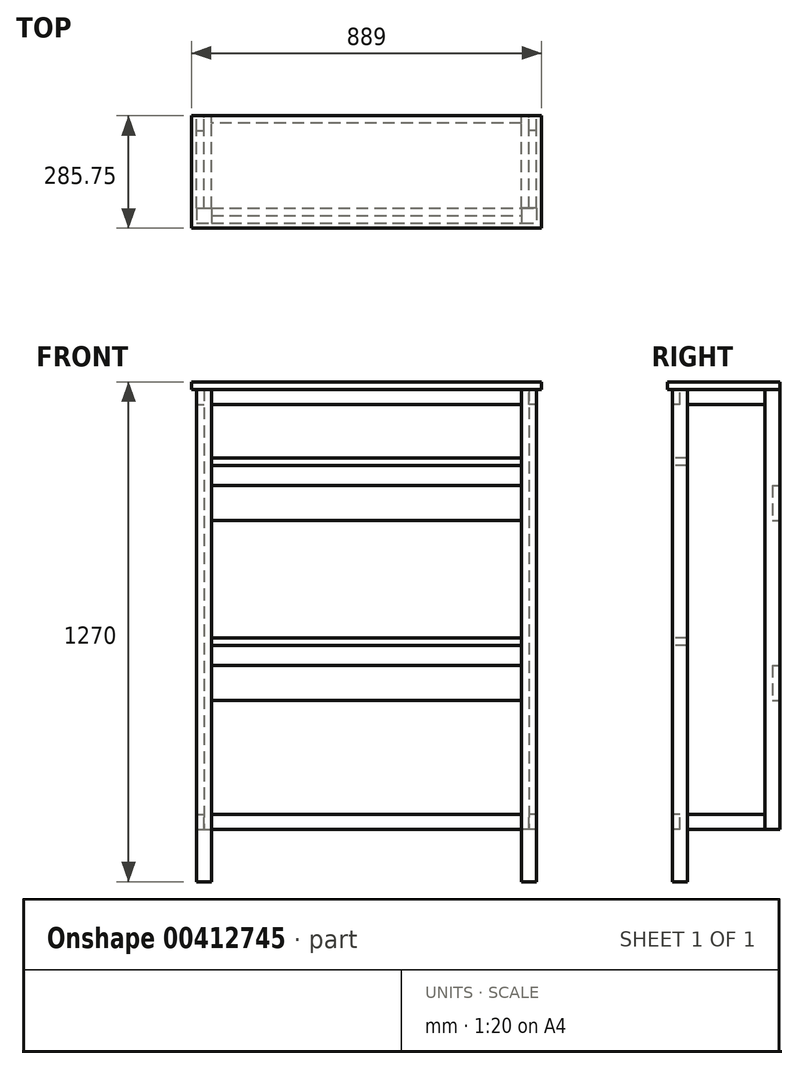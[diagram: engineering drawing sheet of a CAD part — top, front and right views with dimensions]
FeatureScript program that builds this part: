
annotation { "Feature Type Name" : "Feature", "Feature Type Description" : "" }
export const myFeature = defineFeature(function(context is Context, id is Id, definition is map)
    precondition{}
    {
        {
            var Q0;
            Q0=qCreatedBy(makeId("Front.planeOp"),FACE);
            var sketch = newSketch(context, id + "F0", { "sketchPlane" : qUnion([Q0])});
            skLineSegment(sketch, "E0.bottom", {"start": v(0, 0) * mm, "end": v(38.1, 0) * mm});
            skLineSegment(sketch, "E0.top", {"start": v(0, 1250.95) * mm, "end": v(38.1, 1250.95) * mm});
            skLineSegment(sketch, "E0.left", {"start": v(0, 0) * mm, "end": v(0, 1250.95) * mm});
            skLineSegment(sketch, "E0.right", {"start": v(38.1, 0) * mm, "end": v(38.1, 1250.95) * mm});
            skSolve(sketch);
        }
        {
            var Q0;
            Q0=makeQuery(id+"F0.imprint","IMPRINT",FACE,{"disambiguationData":[TD([[makeQuery(id+"F0.imprint","IMPRINT",EDGE,{"derivedFrom":sQuery(id+"F0.wireOp",EDGE,"E0.bottom")}),1.0]])]});
            extrude(context, id + "F1", {"entities" : qUnion([Q0]), "oppositeDirection" : true, "depth" : 38.1 * mm});
        }
        {
            var Q0;
            Q0=makeQuery(id+"F1.opExtrude","SWEPT_FACE",FACE,{"disambiguationData":[OSD([sQuery(id+"F0.wireOp",EDGE,"E0.right")])]});
            var sketch = newSketch(context, id + "F2", { "sketchPlane" : qUnion([Q0])});
            skLineSegment(sketch, "E1.bottom", {"start": v(38.1, 1250.95) * mm, "end": v(273.05, 1250.95) * mm});
            skLineSegment(sketch, "E1.top", {"start": v(38.1, 133.35) * mm, "end": v(273.05, 133.35) * mm});
            skLineSegment(sketch, "E1.left", {"start": v(38.1, 1250.95) * mm, "end": v(38.1, 133.35) * mm});
            skLineSegment(sketch, "E1.right", {"start": v(273.05, 1250.95) * mm, "end": v(273.05, 133.35) * mm});
            skSolve(sketch);
        }
        {
            var Q0;
            Q0=makeQuery(id+"F2.imprint","IMPRINT",FACE,{"disambiguationData":[TD([[makeQuery(id+"F2.imprint","IMPRINT",EDGE,{"derivedFrom":sQuery(id+"F2.wireOp",EDGE,"E1.bottom")}),-1.0]])]});
            extrude(context, id + "F3", {"entities" : qUnion([Q0]), "oppositeDirection" : true, "depth" : 19.05 * mm});
        }
        {
            var Q0;
            Q0=makeQuery(id+"F3.opExtrude","CAP_FACE",FACE,{"disambiguationData":[OSD([sQuery(id+"F2.wireOp",EDGE,"E1.bottom"),sQuery(id+"F2.wireOp",EDGE,"E1.top"),sQuery(id+"F2.wireOp",EDGE,"E1.left"),sQuery(id+"F2.wireOp",EDGE,"E1.right")])],"isStart":false});
            var sketch = newSketch(context, id + "F4", { "sketchPlane" : qUnion([Q0])});
            skLineSegment(sketch, "E2.bottom", {"start": v(-273.05, 1250.95) * mm, "end": v(-234.95, 1250.95) * mm});
            skLineSegment(sketch, "E2.top", {"start": v(-273.05, 133.35) * mm, "end": v(-234.95, 133.35) * mm});
            skLineSegment(sketch, "E2.left", {"start": v(-273.05, 1250.95) * mm, "end": v(-273.05, 133.35) * mm});
            skLineSegment(sketch, "E2.right", {"start": v(-234.95, 1250.95) * mm, "end": v(-234.95, 133.35) * mm});
            skSolve(sketch);
        }
        {
            var Q0;
            Q0=makeQuery(id+"F4.imprint","IMPRINT",FACE,{"disambiguationData":[TD([[makeQuery(id+"F4.imprint","IMPRINT",EDGE,{"derivedFrom":sQuery(id+"F4.wireOp",EDGE,"E2.bottom")}),1.0]])]});
            extrude(context, id + "F5", {"entities" : qUnion([Q0]), "depth" : 19.05 * mm});
        }
        {
            var Q0;
            Q0=makeQuery(id+"F3.opExtrude","CAP_FACE",FACE,{"disambiguationData":[OSD([sQuery(id+"F2.wireOp",EDGE,"E1.bottom"),sQuery(id+"F2.wireOp",EDGE,"E1.top"),sQuery(id+"F2.wireOp",EDGE,"E1.left"),sQuery(id+"F2.wireOp",EDGE,"E1.right")])],"isStart":false});
            var sketch = newSketch(context, id + "F6", { "sketchPlane" : qUnion([Q0])});
            skLineSegment(sketch, "E3.bottom", {"start": v(-234.95, 1250.95) * mm, "end": v(-38.1, 1250.95) * mm});
            skLineSegment(sketch, "E3.top", {"start": v(-234.95, 1212.85) * mm, "end": v(-38.1, 1212.85) * mm});
            skLineSegment(sketch, "E3.left", {"start": v(-234.95, 1250.95) * mm, "end": v(-234.95, 1212.85) * mm});
            skLineSegment(sketch, "E3.right", {"start": v(-38.1, 1250.95) * mm, "end": v(-38.1, 1212.85) * mm});
            skSolve(sketch);
        }
        {
            var Q0;
            Q0=makeQuery(id+"F6.imprint","IMPRINT",FACE,{"disambiguationData":[TD([[makeQuery(id+"F6.imprint","IMPRINT",EDGE,{"derivedFrom":sQuery(id+"F6.wireOp",EDGE,"E3.bottom")}),1.0]])]});
            extrude(context, id + "F7", {"entities" : qUnion([Q0]), "depth" : 19.05 * mm});
        }
        {
            var Q0;
            Q0=makeQuery(id+"F3.opExtrude","CAP_FACE",FACE,{"disambiguationData":[OSD([sQuery(id+"F2.wireOp",EDGE,"E1.bottom"),sQuery(id+"F2.wireOp",EDGE,"E1.top"),sQuery(id+"F2.wireOp",EDGE,"E1.left"),sQuery(id+"F2.wireOp",EDGE,"E1.right")])],"isStart":false});
            var sketch = newSketch(context, id + "F8", { "sketchPlane" : qUnion([Q0])});
            skLineSegment(sketch, "E4.bottom", {"start": v(-38.1, 133.35) * mm, "end": v(-234.95, 133.35) * mm});
            skLineSegment(sketch, "E4.top", {"start": v(-38.1, 171.45) * mm, "end": v(-234.95, 171.45) * mm});
            skLineSegment(sketch, "E4.left", {"start": v(-38.1, 133.35) * mm, "end": v(-38.1, 171.45) * mm});
            skLineSegment(sketch, "E4.right", {"start": v(-234.95, 133.35) * mm, "end": v(-234.95, 171.45) * mm});
            skSolve(sketch);
        }
        {
            var Q0;
            Q0=makeQuery(id+"F8.imprint","IMPRINT",FACE,{"disambiguationData":[TD([[makeQuery(id+"F8.imprint","IMPRINT",EDGE,{"derivedFrom":sQuery(id+"F8.wireOp",EDGE,"E4.bottom")}),-1.0]])]});
            extrude(context, id + "F9", {"entities" : qUnion([Q0]), "depth" : 19.05 * mm});
        }
        {
            var Q0;
            Q0=qCreatedBy(makeId("Front.planeOp"),FACE);
            var sketch = newSketch(context, id + "F10", { "sketchPlane" : qUnion([Q0])});
            skLineSegment(sketch, "E5.bottom", {"start": v(825.5, 0) * mm, "end": v(863.6, 0) * mm});
            skLineSegment(sketch, "E5.top", {"start": v(825.5, 1250.95) * mm, "end": v(863.6, 1250.95) * mm});
            skLineSegment(sketch, "E5.left", {"start": v(825.5, 0) * mm, "end": v(825.5, 1250.95) * mm});
            skLineSegment(sketch, "E5.right", {"start": v(863.6, 0) * mm, "end": v(863.6, 1250.95) * mm});
            skSolve(sketch);
        }
        {
            var Q0;
            Q0=makeQuery(id+"F10.imprint","IMPRINT",FACE,{"disambiguationData":[TD([[makeQuery(id+"F10.imprint","IMPRINT",EDGE,{"derivedFrom":sQuery(id+"F10.wireOp",EDGE,"E5.bottom")}),1.0]])]});
            extrude(context, id + "F11", {"entities" : qUnion([Q0]), "oppositeDirection" : true, "depth" : 38.1 * mm});
        }
        {
            var Q0;
            Q0=makeQuery(id+"F11.opExtrude","SWEPT_FACE",FACE,{"disambiguationData":[OSD([sQuery(id+"F10.wireOp",EDGE,"E5.left")])]});
            var sketch = newSketch(context, id + "F12", { "sketchPlane" : qUnion([Q0])});
            skLineSegment(sketch, "E6.bottom", {"start": v(-38.1, 1250.95) * mm, "end": v(-273.05, 1250.95) * mm});
            skLineSegment(sketch, "E6.top", {"start": v(-38.1, 133.35) * mm, "end": v(-273.05, 133.35) * mm});
            skLineSegment(sketch, "E6.left", {"start": v(-38.1, 1250.95) * mm, "end": v(-38.1, 133.35) * mm});
            skLineSegment(sketch, "E6.right", {"start": v(-273.05, 1250.95) * mm, "end": v(-273.05, 133.35) * mm});
            skSolve(sketch);
        }
        {
            var Q0;
            Q0=makeQuery(id+"F12.imprint","IMPRINT",FACE,{"disambiguationData":[TD([[makeQuery(id+"F12.imprint","IMPRINT",EDGE,{"derivedFrom":sQuery(id+"F12.wireOp",EDGE,"E6.bottom")}),1.0]])]});
            extrude(context, id + "F13", {"entities" : qUnion([Q0]), "oppositeDirection" : true, "depth" : 19.05 * mm});
        }
        {
            var Q0;
            Q0=makeQuery(id+"F13.opExtrude","CAP_FACE",FACE,{"disambiguationData":[OSD([sQuery(id+"F12.wireOp",EDGE,"E6.bottom"),sQuery(id+"F12.wireOp",EDGE,"E6.top"),sQuery(id+"F12.wireOp",EDGE,"E6.left"),sQuery(id+"F12.wireOp",EDGE,"E6.right")])],"isStart":false});
            var sketch = newSketch(context, id + "F14", { "sketchPlane" : qUnion([Q0])});
            skLineSegment(sketch, "E7.bottom", {"start": v(273.05, 1250.95) * mm, "end": v(234.95, 1250.95) * mm});
            skLineSegment(sketch, "E7.top", {"start": v(273.05, 133.35) * mm, "end": v(234.95, 133.35) * mm});
            skLineSegment(sketch, "E7.left", {"start": v(273.05, 1250.95) * mm, "end": v(273.05, 133.35) * mm});
            skLineSegment(sketch, "E7.right", {"start": v(234.95, 1250.95) * mm, "end": v(234.95, 133.35) * mm});
            skSolve(sketch);
        }
        {
            var Q0;
            Q0=makeQuery(id+"F14.imprint","IMPRINT",FACE,{"disambiguationData":[TD([[makeQuery(id+"F14.imprint","IMPRINT",EDGE,{"derivedFrom":sQuery(id+"F14.wireOp",EDGE,"E7.bottom")}),-1.0]])]});
            extrude(context, id + "F15", {"entities" : qUnion([Q0]), "depth" : 19.05 * mm});
        }
        {
            var Q0;
            Q0=makeQuery(id+"F13.opExtrude","CAP_FACE",FACE,{"disambiguationData":[OSD([sQuery(id+"F12.wireOp",EDGE,"E6.bottom"),sQuery(id+"F12.wireOp",EDGE,"E6.top"),sQuery(id+"F12.wireOp",EDGE,"E6.left"),sQuery(id+"F12.wireOp",EDGE,"E6.right")])],"isStart":false});
            var sketch = newSketch(context, id + "F16", { "sketchPlane" : qUnion([Q0])});
            skLineSegment(sketch, "E8.bottom", {"start": v(38.1, 1250.95) * mm, "end": v(234.95, 1250.95) * mm});
            skLineSegment(sketch, "E8.top", {"start": v(38.1, 1212.85) * mm, "end": v(234.95, 1212.85) * mm});
            skLineSegment(sketch, "E8.left", {"start": v(38.1, 1250.95) * mm, "end": v(38.1, 1212.85) * mm});
            skLineSegment(sketch, "E8.right", {"start": v(234.95, 1250.95) * mm, "end": v(234.95, 1212.85) * mm});
            skSolve(sketch);
        }
        {
            var Q0;
            Q0=makeQuery(id+"F16.imprint","IMPRINT",FACE,{"disambiguationData":[TD([[makeQuery(id+"F16.imprint","IMPRINT",EDGE,{"derivedFrom":sQuery(id+"F16.wireOp",EDGE,"E8.bottom")}),-1.0]])]});
            extrude(context, id + "F17", {"entities" : qUnion([Q0]), "depth" : 19.05 * mm});
        }
        {
            var Q0;
            Q0=makeQuery(id+"F13.opExtrude","CAP_FACE",FACE,{"disambiguationData":[OSD([sQuery(id+"F12.wireOp",EDGE,"E6.bottom"),sQuery(id+"F12.wireOp",EDGE,"E6.top"),sQuery(id+"F12.wireOp",EDGE,"E6.left"),sQuery(id+"F12.wireOp",EDGE,"E6.right")])],"isStart":false});
            var sketch = newSketch(context, id + "F18", { "sketchPlane" : qUnion([Q0])});
            skLineSegment(sketch, "E9.bottom", {"start": v(38.1, 171.45) * mm, "end": v(234.95, 171.45) * mm});
            skLineSegment(sketch, "E9.top", {"start": v(38.1, 133.35) * mm, "end": v(234.95, 133.35) * mm});
            skLineSegment(sketch, "E9.left", {"start": v(38.1, 171.45) * mm, "end": v(38.1, 133.35) * mm});
            skLineSegment(sketch, "E9.right", {"start": v(234.95, 171.45) * mm, "end": v(234.95, 133.35) * mm});
            skSolve(sketch);
        }
        {
            var Q0;
            Q0=makeQuery(id+"F18.imprint","IMPRINT",FACE,{"disambiguationData":[TD([[makeQuery(id+"F18.imprint","IMPRINT",EDGE,{"derivedFrom":sQuery(id+"F18.wireOp",EDGE,"E9.bottom")}),-1.0]])]});
            extrude(context, id + "F19", {"entities" : qUnion([Q0]), "depth" : 19.05 * mm});
        }
        {
            var Q0;
            Q0=makeQuery(id+"F1.opExtrude","CAP_FACE",FACE,{"disambiguationData":[OSD([sQuery(id+"F0.wireOp",EDGE,"E0.bottom"),sQuery(id+"F0.wireOp",EDGE,"E0.top"),sQuery(id+"F0.wireOp",EDGE,"E0.left"),sQuery(id+"F0.wireOp",EDGE,"E0.right")])],"isStart":true});
            var sketch = newSketch(context, id + "F20", { "sketchPlane" : qUnion([Q0])});
            skLineSegment(sketch, "E10.bottom", {"start": v(38.1, 1250.95) * mm, "end": v(825.5, 1250.95) * mm});
            skLineSegment(sketch, "E10.top", {"start": v(38.1, 1212.85) * mm, "end": v(825.5, 1212.85) * mm});
            skLineSegment(sketch, "E10.left", {"start": v(38.1, 1250.95) * mm, "end": v(38.1, 1212.85) * mm});
            skLineSegment(sketch, "E10.right", {"start": v(825.5, 1250.95) * mm, "end": v(825.5, 1212.85) * mm});
            skSolve(sketch);
        }
        {
            var Q0;
            Q0=makeQuery(id+"F20.imprint","IMPRINT",FACE,{"disambiguationData":[TD([[makeQuery(id+"F20.imprint","IMPRINT",EDGE,{"derivedFrom":sQuery(id+"F20.wireOp",EDGE,"E10.bottom")}),-1.0]])]});
            extrude(context, id + "F21", {"entities" : qUnion([Q0]), "oppositeDirection" : true, "depth" : 19.05 * mm});
        }
        {
            var Q0;
            Q0=makeQuery(id+"F1.opExtrude","CAP_FACE",FACE,{"disambiguationData":[OSD([sQuery(id+"F0.wireOp",EDGE,"E0.bottom"),sQuery(id+"F0.wireOp",EDGE,"E0.top"),sQuery(id+"F0.wireOp",EDGE,"E0.left"),sQuery(id+"F0.wireOp",EDGE,"E0.right")])],"isStart":true});
            var sketch = newSketch(context, id + "F22", { "sketchPlane" : qUnion([Q0])});
            skLineSegment(sketch, "E11.bottom", {"start": v(38.1, 133.35) * mm, "end": v(825.5, 133.35) * mm});
            skLineSegment(sketch, "E11.top", {"start": v(38.1, 171.45) * mm, "end": v(825.5, 171.45) * mm});
            skLineSegment(sketch, "E11.left", {"start": v(38.1, 133.35) * mm, "end": v(38.1, 171.45) * mm});
            skLineSegment(sketch, "E11.right", {"start": v(825.5, 133.35) * mm, "end": v(825.5, 171.45) * mm});
            skSolve(sketch);
        }
        {
            var Q0;
            Q0=makeQuery(id+"F22.imprint","IMPRINT",FACE,{"disambiguationData":[TD([[makeQuery(id+"F22.imprint","IMPRINT",EDGE,{"derivedFrom":sQuery(id+"F22.wireOp",EDGE,"E11.bottom")}),1.0]])]});
            extrude(context, id + "F23", {"entities" : qUnion([Q0]), "oppositeDirection" : true, "depth" : 19.05 * mm});
        }
        {
            var Q0;
            Q0=makeQuery(id+"F1.opExtrude","CAP_FACE",FACE,{"disambiguationData":[OSD([sQuery(id+"F0.wireOp",EDGE,"E0.bottom"),sQuery(id+"F0.wireOp",EDGE,"E0.top"),sQuery(id+"F0.wireOp",EDGE,"E0.left"),sQuery(id+"F0.wireOp",EDGE,"E0.right")])],"isStart":true});
            var sketch = newSketch(context, id + "F24", { "sketchPlane" : qUnion([Q0])});
            skLineSegment(sketch, "E12.bottom", {"start": v(38.1, 600.08) * mm, "end": v(825.5, 600.08) * mm});
            skLineSegment(sketch, "E12.top", {"start": v(38.1, 619.13) * mm, "end": v(825.5, 619.13) * mm});
            skLineSegment(sketch, "E12.left", {"start": v(38.1, 600.08) * mm, "end": v(38.1, 619.13) * mm});
            skLineSegment(sketch, "E12.right", {"start": v(825.5, 600.08) * mm, "end": v(825.5, 619.13) * mm});
            skPoint(sketch, "E13", {"position": v(38.1, 609.6) * mm});
            skSolve(sketch);
        }
        {
            var Q0;
            Q0=makeQuery(id+"F24.imprint","IMPRINT",FACE,{"disambiguationData":[TD([[makeQuery(id+"F24.imprint","IMPRINT",EDGE,{"derivedFrom":sQuery(id+"F24.wireOp",EDGE,"E12.bottom")}),1.0]])]});
            extrude(context, id + "F25", {"entities" : qUnion([Q0]), "oppositeDirection" : true, "depth" : 38.1 * mm});
        }
        {
            var Q0;
            Q0=makeQuery(id+"F1.opExtrude","CAP_FACE",FACE,{"disambiguationData":[OSD([sQuery(id+"F0.wireOp",EDGE,"E0.bottom"),sQuery(id+"F0.wireOp",EDGE,"E0.top"),sQuery(id+"F0.wireOp",EDGE,"E0.left"),sQuery(id+"F0.wireOp",EDGE,"E0.right")])],"isStart":true});
            var sketch = newSketch(context, id + "F26", { "sketchPlane" : qUnion([Q0])});
            skLineSegment(sketch, "E14.bottom", {"start": v(38.1, 1076.33) * mm, "end": v(825.5, 1076.33) * mm});
            skLineSegment(sketch, "E14.top", {"start": v(38.1, 1057.28) * mm, "end": v(825.5, 1057.28) * mm});
            skLineSegment(sketch, "E14.left", {"start": v(38.1, 1076.33) * mm, "end": v(38.1, 1057.28) * mm});
            skLineSegment(sketch, "E14.right", {"start": v(825.5, 1076.33) * mm, "end": v(825.5, 1057.28) * mm});
            skPoint(sketch, "E15", {"position": v(38.1, 1066.8) * mm});
            skSolve(sketch);
        }
        {
            var Q0;
            Q0=makeQuery(id+"F26.imprint","IMPRINT",FACE,{"disambiguationData":[TD([[makeQuery(id+"F26.imprint","IMPRINT",EDGE,{"derivedFrom":sQuery(id+"F26.wireOp",EDGE,"E14.bottom")}),-1.0]])]});
            extrude(context, id + "F27", {"entities" : qUnion([Q0]), "oppositeDirection" : true, "depth" : 38.1 * mm});
        }
        {
            var Q0;
            Q0=makeQuery(id+"F3.opExtrude","SWEPT_FACE",FACE,{"disambiguationData":[OSD([sQuery(id+"F2.wireOp",EDGE,"E1.right")])]});
            var sketch = newSketch(context, id + "F28", { "sketchPlane" : qUnion([Q0])});
            skLineSegment(sketch, "E16.bottom", {"start": v(-825.5, 1006.48) * mm, "end": v(-38.1, 1006.48) * mm});
            skLineSegment(sketch, "E16.top", {"start": v(-825.5, 917.58) * mm, "end": v(-38.1, 917.58) * mm});
            skLineSegment(sketch, "E16.left", {"start": v(-825.5, 1006.48) * mm, "end": v(-825.5, 917.58) * mm});
            skLineSegment(sketch, "E16.right", {"start": v(-38.1, 1006.48) * mm, "end": v(-38.1, 917.58) * mm});
            skSolve(sketch);
        }
        {
            var Q0;
            Q0=makeQuery(id+"F28.imprint","IMPRINT",FACE,{"disambiguationData":[TD([[makeQuery(id+"F28.imprint","IMPRINT",EDGE,{"derivedFrom":sQuery(id+"F28.wireOp",EDGE,"E16.bottom")}),-1.0]])]});
            extrude(context, id + "F29", {"entities" : qUnion([Q0]), "oppositeDirection" : true, "depth" : 19.05 * mm});
        }
        {
            var Q0;
            Q0=makeQuery(id+"F13.opExtrude","SWEPT_FACE",FACE,{"disambiguationData":[OSD([sQuery(id+"F12.wireOp",EDGE,"E6.right")])]});
            var sketch = newSketch(context, id + "F30", { "sketchPlane" : qUnion([Q0])});
            skLineSegment(sketch, "E17.bottom", {"start": v(-825.5, 549.28) * mm, "end": v(-38.1, 549.28) * mm});
            skLineSegment(sketch, "E17.top", {"start": v(-825.5, 460.38) * mm, "end": v(-38.1, 460.38) * mm});
            skLineSegment(sketch, "E17.left", {"start": v(-825.5, 549.28) * mm, "end": v(-825.5, 460.38) * mm});
            skLineSegment(sketch, "E17.right", {"start": v(-38.1, 549.28) * mm, "end": v(-38.1, 460.38) * mm});
            skSolve(sketch);
        }
        {
            var Q0;
            Q0=makeQuery(id+"F30.imprint","IMPRINT",FACE,{"disambiguationData":[TD([[makeQuery(id+"F30.imprint","IMPRINT",EDGE,{"derivedFrom":sQuery(id+"F30.wireOp",EDGE,"E17.bottom")}),-1.0]])]});
            extrude(context, id + "F31", {"entities" : qUnion([Q0]), "oppositeDirection" : true, "depth" : 19.05 * mm});
        }
        {
            var Q0;
            Q0=makeQuery(id+"F1.opExtrude","SWEPT_FACE",FACE,{"disambiguationData":[OSD([sQuery(id+"F0.wireOp",EDGE,"E0.top")])]});
            var sketch = newSketch(context, id + "F32", { "sketchPlane" : qUnion([Q0])});
            skLineSegment(sketch, "E18.bottom", {"start": v(-12.7, 273.05) * mm, "end": v(876.3, 273.05) * mm});
            skLineSegment(sketch, "E18.top", {"start": v(-12.7, -12.7) * mm, "end": v(876.3, -12.7) * mm});
            skLineSegment(sketch, "E18.left", {"start": v(-12.7, 273.05) * mm, "end": v(-12.7, -12.7) * mm});
            skLineSegment(sketch, "E18.right", {"start": v(876.3, 273.05) * mm, "end": v(876.3, -12.7) * mm});
            skSolve(sketch);
        }
        {
            var Q0;
            Q0=makeQuery(id+"F32.imprint","IMPRINT",FACE,{"disambiguationData":[TD([[makeQuery(id+"F32.imprint","IMPRINT",EDGE,{"derivedFrom":sQuery(id+"F32.wireOp",EDGE,"E18.bottom")}),-1.0]])]});
            var Q1;
            {var subQ0=sQuery(id+"F0.wireOp",EDGE,"E0.top");Q1=makeQuery(id+"F32.imprint","IMPRINT",FACE,{"disambiguationData":[TD([[makeQuery(id+"F32.imprint","IMPRINT",EDGE,{"derivedFrom":makeQuery(id+"F1.opExtrude","CAP_EDGE",EDGE,{"disambiguationData":[OSD([subQ0])],"isStart":true})}),1.0]])]});}
            extrude(context, id + "F33", {"entities" : qUnion([Q0, Q1]), "depth" : 19.05 * mm});
        }
    });
